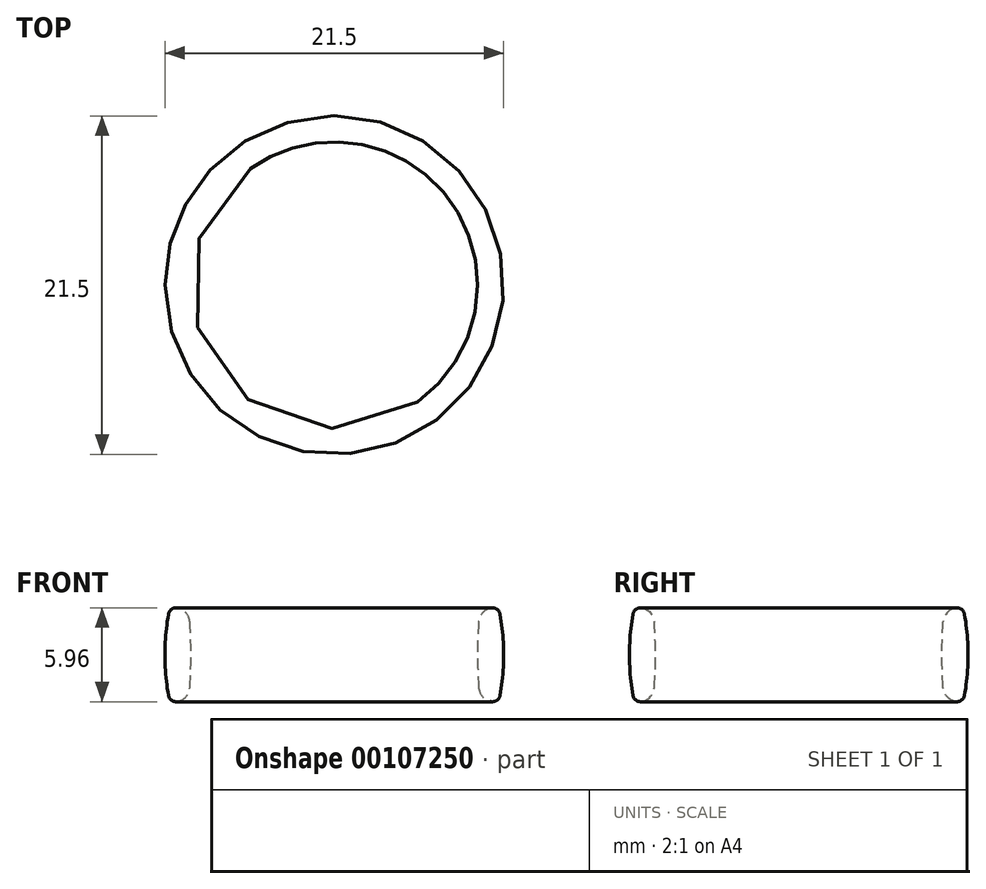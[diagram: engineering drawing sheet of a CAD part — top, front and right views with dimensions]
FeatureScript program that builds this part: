
annotation { "Feature Type Name" : "Feature", "Feature Type Description" : "" }
export const myFeature = defineFeature(function(context is Context, id is Id, definition is map)
    precondition{}
    {
        {
            var Q0;
            Q0=qCreatedBy(makeId("Top.planeOp"),FACE);
            var sketch = newSketch(context, id + "F0", { "sketchPlane" : qUnion([Q0])});
            skEllipse(sketch, "E0", {"center": v(0, 0) * mm, "majorRadius": 9.1 * mm, "minorRadius": 9.1 * mm, "majorAxis": v(1, 0)});
            skSolve(sketch);
        }
        {
            var Q0;
            Q0=qCreatedBy(makeId("Front.planeOp"),FACE);
            var sketch = newSketch(context, id + "F1", { "sketchPlane" : qUnion([Q0])});
            skLineSegment(sketch, "E1.bottom", {"start": v(9.25, 3) * mm, "end": v(10.45, 3) * mm});
            skLineSegment(sketch, "E1.top", {"start": v(9.25, -3) * mm, "end": v(10.45, -3) * mm});
            skLineSegment(sketch, "E1.left", {"start": v(9.25, 3) * mm, "end": v(9.25, -3) * mm, "construction": true});
            skLineSegment(sketch, "E1.right", {"start": v(10.45, 3) * mm, "end": v(10.45, -3) * mm, "construction": true});
            skLineSegment(sketch, "E2", {"start": v(0, 0) * mm, "end": v(9.1, 0) * mm, "construction": true});
            skArc(sketch, "E3", {"start": v(9.25, 3) * mm, "mid": v(9.1, 0) * mm, "end": v(9.25, -3) * mm});
            skArc(sketch, "E4", {"start": v(10.45, -3) * mm, "mid": v(10.75, 0) * mm, "end": v(10.45, 3) * mm});
            skSolve(sketch);
        }
        {
            var Q0;
            Q0=makeQuery(id+"F1.imprint","IMPRINT",FACE,{"disambiguationData":[TD([[makeQuery(id+"F1.imprint","IMPRINT",EDGE,{"derivedFrom":sQuery(id+"F1.wireOp",EDGE,"E1.bottom")}),-1.0]])]});
            var Q1;
            Q1 = qConstructionFilter(qBodyType(qCreatedBy(id + "F0" ,EDGE), BodyType.WIRE), ConstructionObject.NO);
            sweep(context, id + "F2", {"profiles" : qUnion([Q0]), "path" : qUnion([Q1])});
        }
        {
            var Q0;
            Q0=makeQuery(id+"F2.opSweep","SWEPT_EDGE",EDGE,{"disambiguationData":[OSD([sQuery(id+"F0.wireOp",EDGE,"E0"),sQuery(id+"F1.wireOp",EDGE,"E1.bottom"),sQuery(id+"F1.wireOp",EDGE,"E3")])]});
            var Q1;
            Q1=makeQuery(id+"F2.opSweep","SWEPT_EDGE",EDGE,{"disambiguationData":[OSD([sQuery(id+"F0.wireOp",EDGE,"E0"),sQuery(id+"F1.wireOp",EDGE,"E1.top"),sQuery(id+"F1.wireOp",EDGE,"E3")])]});
            fillet(context, id + "F3", {"entities" : qUnion([Q0, Q1]), "radius" : 1 * mm, "tangentPropagation" : true, "allowEdgeOverflow" : false});
        }
        {
            var Q0;
            Q0=makeQuery(id+"F2.opSweep","SWEPT_EDGE",EDGE,{"disambiguationData":[OSD([sQuery(id+"F0.wireOp",EDGE,"E0"),sQuery(id+"F1.wireOp",EDGE,"E1.bottom"),sQuery(id+"F1.wireOp",EDGE,"E4")])]});
            var Q1;
            Q1=makeQuery(id+"F2.opSweep","SWEPT_EDGE",EDGE,{"disambiguationData":[OSD([sQuery(id+"F0.wireOp",EDGE,"E0"),sQuery(id+"F1.wireOp",EDGE,"E1.top"),sQuery(id+"F1.wireOp",EDGE,"E4")])]});
            fillet(context, id + "F4", {"entities" : qUnion([Q0, Q1]), "radius" : 0.5 * mm, "tangentPropagation" : true, "allowEdgeOverflow" : false});
        }
    });
